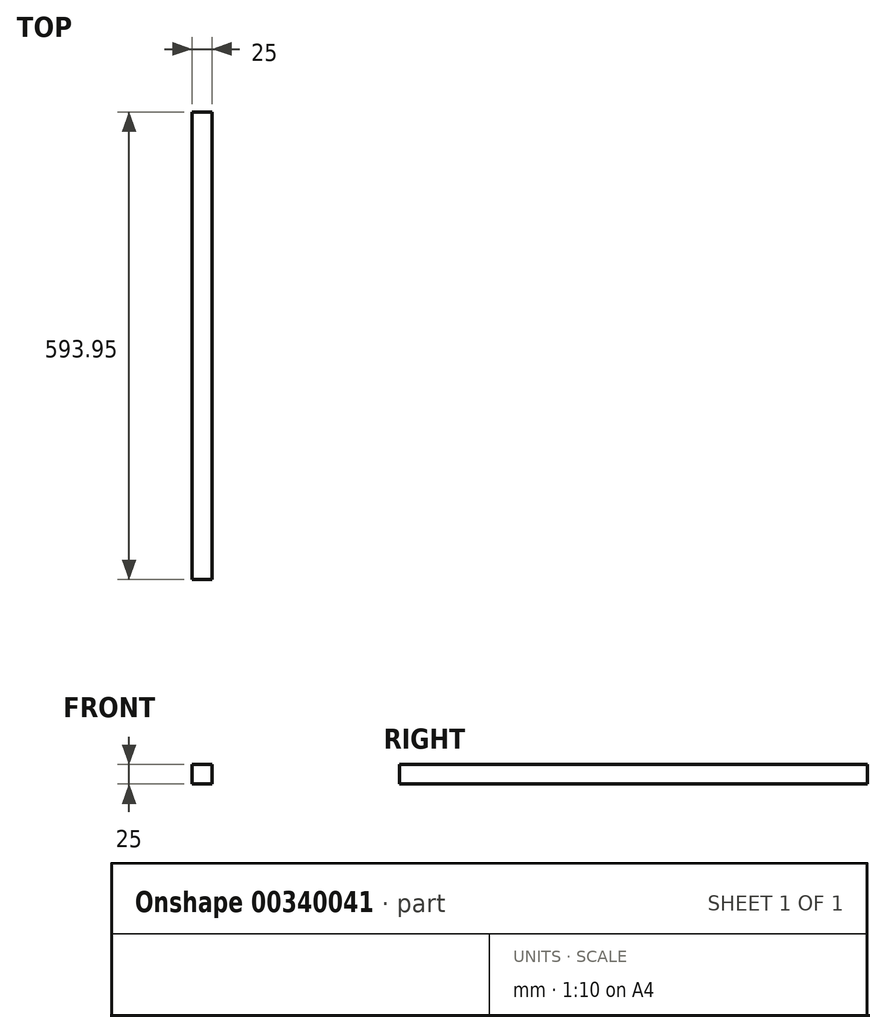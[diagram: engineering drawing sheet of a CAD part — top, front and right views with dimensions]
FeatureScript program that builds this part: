
annotation { "Feature Type Name" : "Feature", "Feature Type Description" : "" }
export const myFeature = defineFeature(function(context is Context, id is Id, definition is map)
    precondition{}
    {
        {
            var Q0;
            Q0=qCreatedBy(makeId("Front.planeOp"),FACE);
            var sketch = newSketch(context, id + "F0", { "sketchPlane" : qUnion([Q0])});
            skLineSegment(sketch, "E0.bottom", {"start": v(-9.87, 7.33) * mm, "end": v(15.13, 7.33) * mm});
            skLineSegment(sketch, "E0.top", {"start": v(-9.87, -17.67) * mm, "end": v(15.13, -17.67) * mm});
            skLineSegment(sketch, "E0.left", {"start": v(-9.87, 7.33) * mm, "end": v(-9.87, -17.67) * mm});
            skLineSegment(sketch, "E0.right", {"start": v(15.13, 7.33) * mm, "end": v(15.13, -17.67) * mm});
            skSolve(sketch);
        }
        {
            var Q0;
            Q0 = qSketchRegion(id + "F0", true);
            extrude(context, id + "F1", {"entities" : qUnion([Q0]), "depth" : 593.95 * mm});
        }
    });
